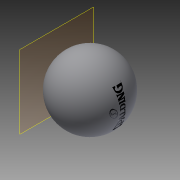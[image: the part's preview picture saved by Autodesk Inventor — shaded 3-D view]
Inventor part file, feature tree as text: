
AUTODESK INVENTOR PART (.ipt)
format: ipt  version: 2015 (Build 190159000, 159)  size: 168,960 bytes
history: native  units: mm
features: other x2, sketch x2, revolve x1, plane x1
ambient origin geometry x8: Origin, YZ Plane, XZ Plane, XY Plane, X Axis, Y Axis, Z Axis, Center Point
bodies: Solid1 (feature_tree)
feature tree (6):
  revolve  "Revolution1"  [1 undecoded]
  plane  "Work Plane1"
  other  "Decal1"
  sketch  "Sketch1"  dims[d0=220.0mm d1=3.490659mm]
  sketch  "Sketch2"
  other  "Image1"
note: 1 required parameter value undecoded (feature->parameter linkage not recoverable at this tier; creation-order binding heuristic only, values carry confidence <= 0.55)
